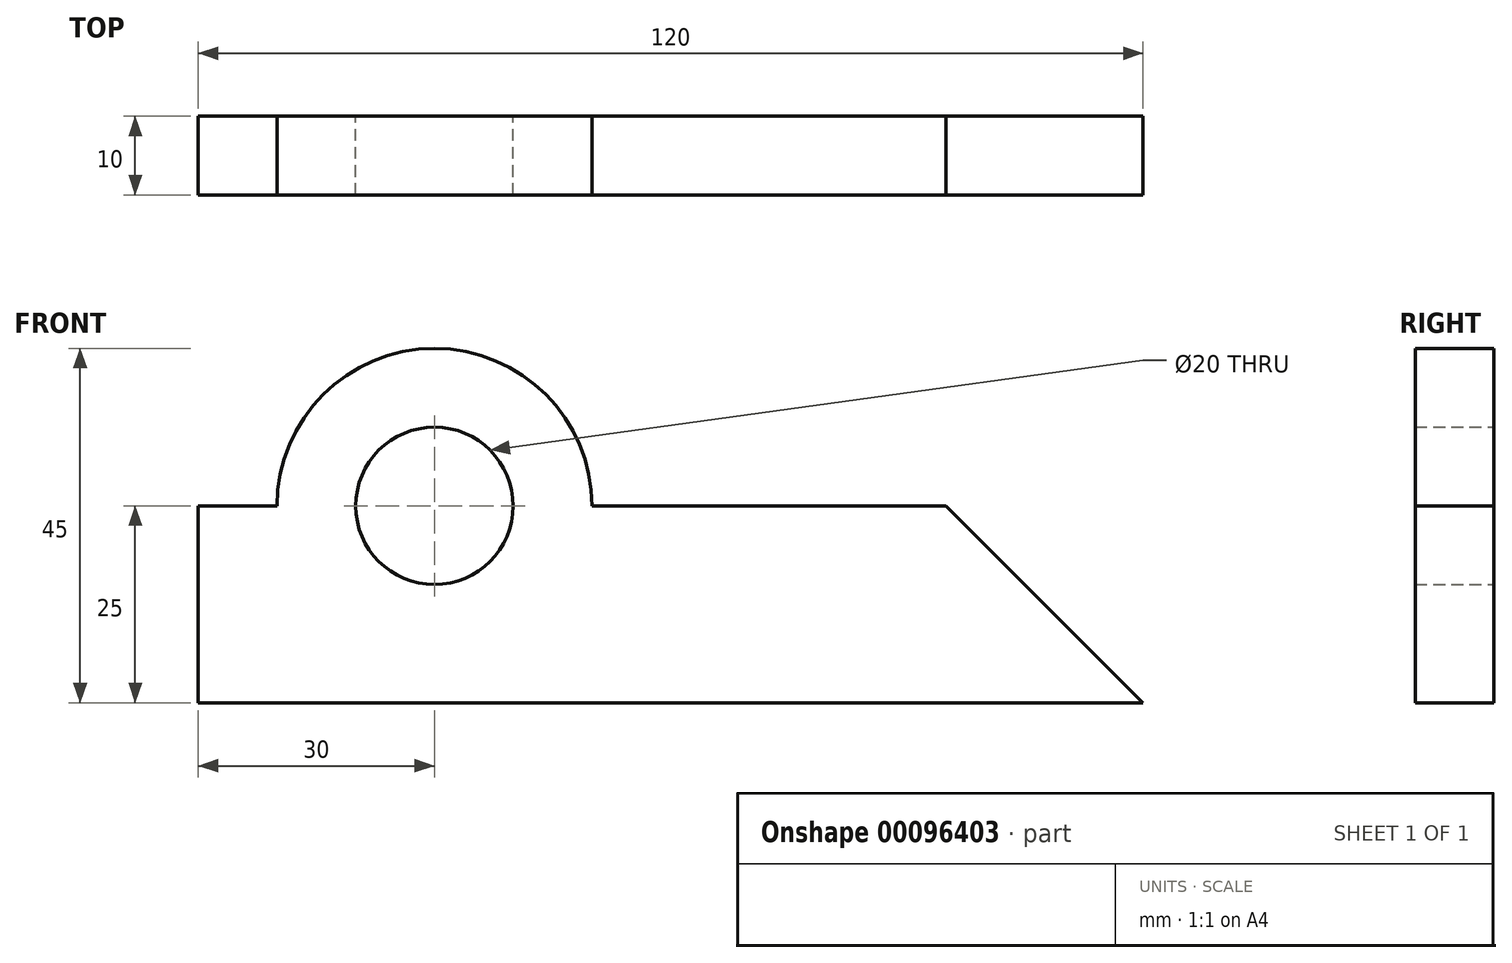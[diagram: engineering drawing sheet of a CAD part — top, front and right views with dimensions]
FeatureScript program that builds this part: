
annotation { "Feature Type Name" : "Feature", "Feature Type Description" : "" }
export const myFeature = defineFeature(function(context is Context, id is Id, definition is map)
    precondition{}
    {
        {
            var Q0;
            Q0=qCreatedBy(makeId("Front.planeOp"),FACE);
            var sketch = newSketch(context, id + "F0", { "sketchPlane" : qUnion([Q0])});
            skLineSegment(sketch, "E0", {"start": v(0, 0) * mm, "end": v(120, 0) * mm});
            skLineSegment(sketch, "E1", {"start": v(0, 0) * mm, "end": v(0, 25) * mm});
            skLineSegment(sketch, "E2", {"start": v(120, 0) * mm, "end": v(95, 25) * mm});
            skCircle(sketch, "E3", {"center": v(30, 25) * mm, "radius": 10 * mm});
            skLineSegment(sketch, "E4", {"start": v(95, 25) * mm, "end": v(50, 25) * mm});
            skLineSegment(sketch, "E5", {"start": v(0, 25) * mm, "end": v(10, 25) * mm});
            skArc(sketch, "E6", {"start": v(50, 25) * mm, "mid": v(30, 45) * mm, "end": v(10, 25) * mm});
            skSolve(sketch);
        }
        {
            var Q0;
            Q0 = qSketchRegion(id + "F0", true);
            extrude(context, id + "F1", {"entities" : qUnion([Q0]), "depth" : 10 * mm});
        }
    });
